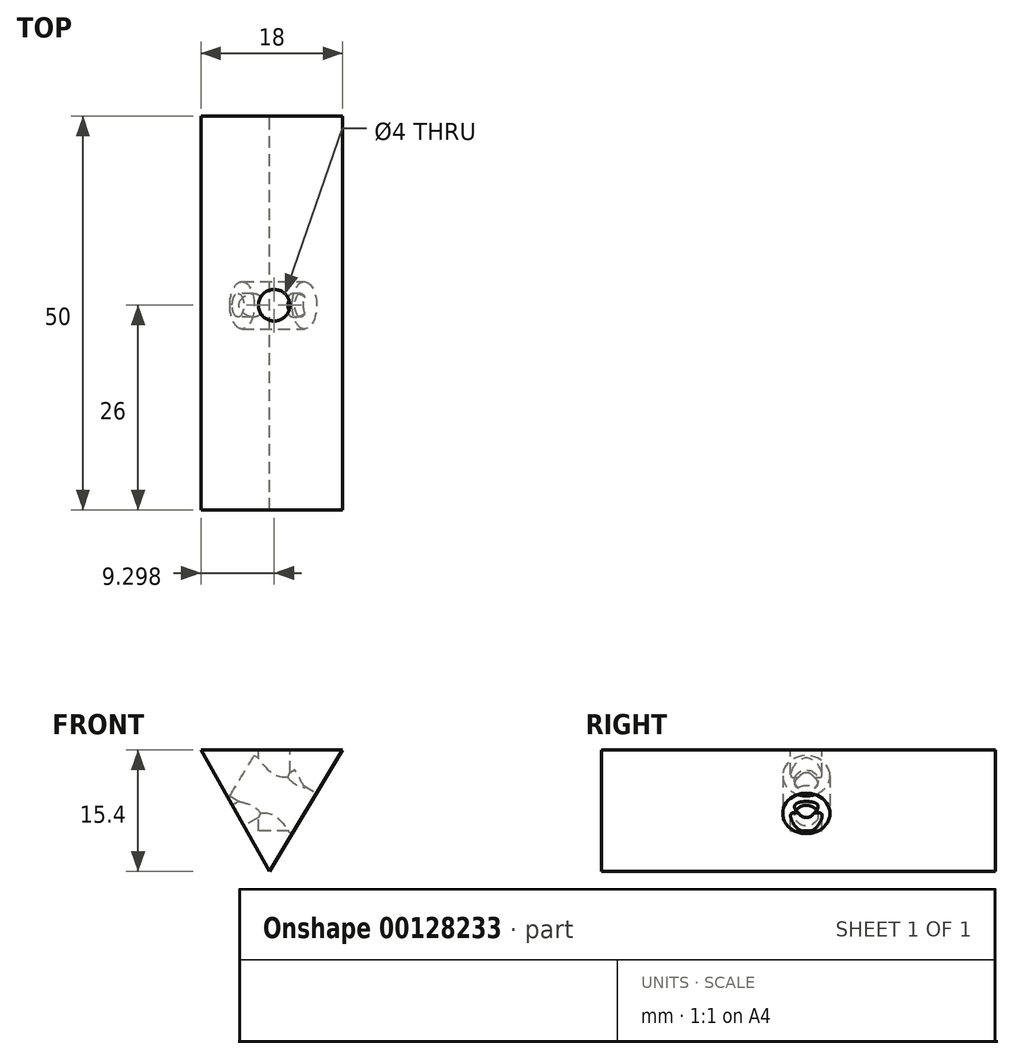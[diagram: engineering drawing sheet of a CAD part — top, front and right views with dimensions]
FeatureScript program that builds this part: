
annotation { "Feature Type Name" : "Feature", "Feature Type Description" : "" }
export const myFeature = defineFeature(function(context is Context, id is Id, definition is map)
    precondition{}
    {
        {
            var Q0;
            Q0=qCreatedBy(makeId("Front.planeOp"),FACE);
            var sketch = newSketch(context, id + "F0", { "sketchPlane" : qUnion([Q0])});
            skLineSegment(sketch, "E0", {"start": v(-0.6, -9.66) * mm, "end": v(8.7, 5.74) * mm});
            skLineSegment(sketch, "E1", {"start": v(8.7, 5.74) * mm, "end": v(-9.3, 5.73) * mm});
            skLineSegment(sketch, "E2", {"start": v(-9.3, 5.73) * mm, "end": v(-0.6, -9.66) * mm});
            skSolve(sketch);
        }
        {
            var Q0;
            Q0=makeQuery(id+"F0.imprint","IMPRINT",FACE,{"disambiguationData":[TD([[makeQuery(id+"F0.imprint","IMPRINT",EDGE,{"derivedFrom":sQuery(id+"F0.wireOp",EDGE,"E0")}),1.0]])]});
            extrude(context, id + "F1", {"entities" : qUnion([Q0]), "depth" : 50 * mm});
        }
        {
            var Q0;
            Q0=makeQuery(id+"F1.opExtrude","SWEPT_FACE",FACE,{"disambiguationData":[OSD([sQuery(id+"F0.wireOp",EDGE,"E0")])]});
            var sketch = newSketch(context, id + "F2", { "sketchPlane" : qUnion([Q0])});
            skCircle(sketch, "E3", {"center": v(-24, 0) * mm, "radius": 3 * mm});
            skSolve(sketch);
        }
        {
            var Q0;
            Q0=makeQuery(id+"F1.opExtrude","SWEPT_FACE",FACE,{"disambiguationData":[OSD([sQuery(id+"F0.wireOp",EDGE,"E1")])]});
            var sketch = newSketch(context, id + "F3", { "sketchPlane" : qUnion([Q0])});
            skCircle(sketch, "E4", {"center": v(0, -24) * mm, "radius": 2 * mm});
            skSolve(sketch);
        }
        {
            var Q0;
            Q0=makeQuery(id+"F1.opExtrude","SWEPT_FACE",FACE,{"disambiguationData":[OSD([sQuery(id+"F0.wireOp",EDGE,"E2")])]});
            var sketch = newSketch(context, id + "F4", { "sketchPlane" : qUnion([Q0])});
            skCircle(sketch, "E5", {"center": v(24, 0) * mm, "radius": 1.5 * mm});
            skSolve(sketch);
        }
        {
            var Q0;
            Q0=makeQuery(id+"F2.imprint","IMPRINT",FACE,{"disambiguationData":[TD([[makeQuery(id+"F2.imprint","IMPRINT",EDGE,{"derivedFrom":sQuery(id+"F2.wireOp",EDGE,"E3")}),1.0]])]});
            extrude(context, id + "F5", {"entities" : qUnion([Q0]), "operationType" : NewBodyOperationType.REMOVE, "oppositeDirection" : true, "depth" : 9.25 * mm});
        }
        {
            var Q0;
            Q0=makeQuery(id+"F3.imprint","IMPRINT",FACE,{"disambiguationData":[TD([[makeQuery(id+"F3.imprint","IMPRINT",EDGE,{"derivedFrom":sQuery(id+"F3.wireOp",EDGE,"E4")}),1.0]])]});
            extrude(context, id + "F6", {"entities" : qUnion([Q0]), "operationType" : NewBodyOperationType.REMOVE, "oppositeDirection" : true, "depth" : 10.3 * mm});
        }
        {
            var Q0;
            Q0=makeQuery(id+"F4.imprint","IMPRINT",FACE,{"disambiguationData":[TD([[makeQuery(id+"F4.imprint","IMPRINT",EDGE,{"derivedFrom":sQuery(id+"F4.wireOp",EDGE,"E5")}),1.0]])]});
            extrude(context, id + "F7", {"entities" : qUnion([Q0]), "operationType" : NewBodyOperationType.REMOVE, "oppositeDirection" : true, "depth" : 9.13 * mm});
        }
    });
